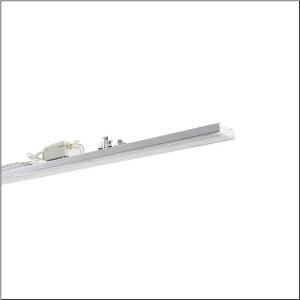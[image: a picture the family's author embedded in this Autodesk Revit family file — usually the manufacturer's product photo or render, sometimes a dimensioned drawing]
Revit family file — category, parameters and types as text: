
# Revit family: licross_r__21_recessed_mo_52tl1ecn485g_7a1e
name_source: partatom
category: Lighting Fixtures
units: mm (PartAtom-declared; Revit-internal decimal feet)

## family parameters
Cut with Voids When Loaded = No
Host = Face
Light Source = No
Part Type = Normal
Room Calculation Point = No
Round Connector Dimension = Use Diameter
Shared = No

## types (1)
- --- (1 x LED, 8960 lm, 49.9 W, 4000K)
    Apparent Load = 50 VA
    CIE Flux Codes = 85 95 99 100 100
    Color Rendering = 80
    Color Temperature = 4000K
    Default Elevation = 1800 mm
    Description = Licross® 21 Recessed MO, luminaire insert, of sheet steel, galvanised, coil coated, white, length: 1.500mm, width: 66mm, height: 67mm, LED rated luminous flux: 8.960lm, light colour: 840, control gear: ON/OFF Multilumen, CLOi, control gear: ECG Multilumen, with plug, 3-pole, with phase selection, mains connection: 220..240V, AC, 50/60Hz, start of lifetime: 50W, end of service life: 61W, halogen-free wiring, primary light control with lens, of plastic, primary optical cover: cover, of PMMA, light emission: direct distribution, primary light characteristic: symmetric, protection rating (complete): IP40, insulation class (complete): insulation class I (protective earthing), certification: CE, ENEC, VDE, UKCA, protection symbol: D if used in an environment without relevant dust loads with corresponding accessories, impact resistance: IK06, permissible ambient temperature for indoor applications: -35..+40°C, corresponds to IFS (International Featured Standards) requirements for safety and quality in the food industry, reducing of maximum allowable ambient temperature of 5°C with ceiling mounting, LABS conformity tested according to VDMA 24364:2018-05, packaging unit: 1 piece
    Height = 58 mm
    Lamp = 1 x LED
    Lamp Light Flux = 8960 lm
    Lamp Power = 49.9 W
    Lamp count = 1
    Length = 1500 mm
    Luminous efficacy = 180 lm/W
    Manufacturer = Siteco
    ModVariant = No
    Model = 52TL1ECN485G
    Mounting Place = Ceiling
    Mounting Type = Pendant
    Number of Poles = 1
    OnlyDefault = Yes
    Power Factor = 1
    Product Name = Licross® 21 Recessed MO
    Product group = luminaire insert
    ProductGroupID = 901
    Protection Class = Protection class I
    Protection Degree = IP 40
    RLX_Detail_Level = 1
    RLX_Emergency_Light_Flux = 0 lm
    RLX_Emergency_Type = 0
    RLX_Emergency_Type_DB = No
    RlxData = <blob elided: 22425 chars, md5=2c8c6795>
    Socket = socket
    Standby Power = 0 W
    System Light Flux = 8960 lm
    System Power = 50 W
    Type Comments = factory setting: luminous flux: 100 % | (A | C | E) | 116 mA
    Type Image = l_1296930.jpg
    URL = http://relux.com
    VarID = @adj_040097
    Voltage = 0 V
    Weight = 0.00 kg
    Width = 66 mm

## geometry (parser evidence)
native form markers: Blend x4, Sweep x14
no freeform markers — native parametric forms only
